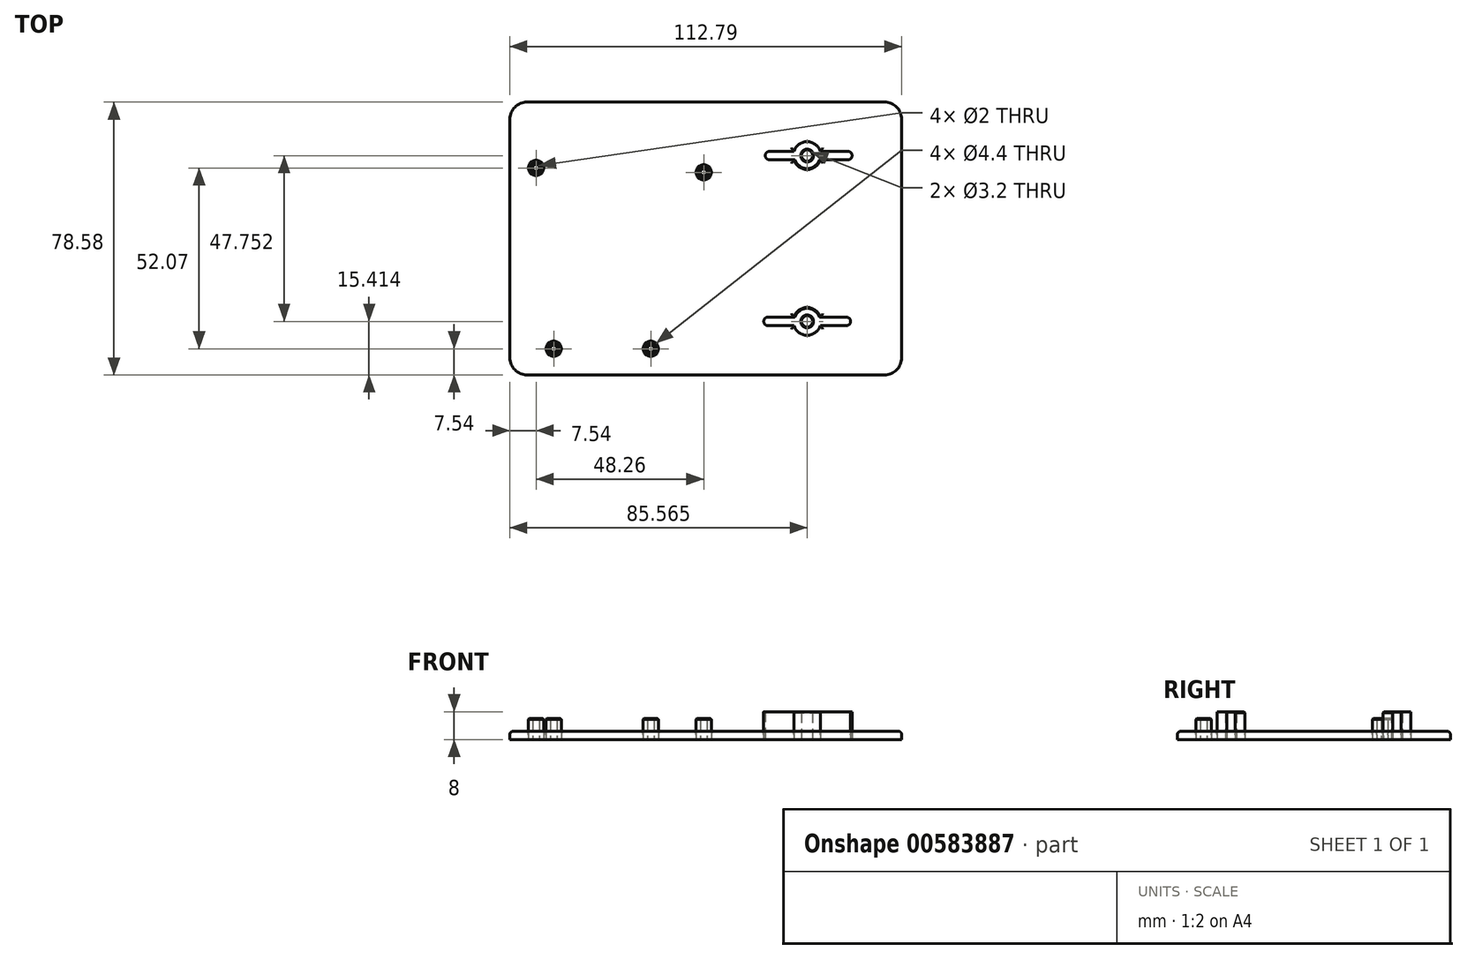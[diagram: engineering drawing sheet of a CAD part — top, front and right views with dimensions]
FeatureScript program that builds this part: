
annotation { "Feature Type Name" : "Feature", "Feature Type Description" : "" }
export const myFeature = defineFeature(function(context is Context, id is Id, definition is map)
    precondition{}
    {
        {
            var Q0;
            Q0=qCreatedBy(makeId("Top.planeOp"),FACE);
            var sketch = newSketch(context, id + "F0", { "sketchPlane" : qUnion([Q0])});
            skLineSegment(sketch, "E0.bottom", {"start": v(0, 0) * mm, "end": v(102.79, 0) * mm});
            skLineSegment(sketch, "E0.top", {"start": v(0, 68.58) * mm, "end": v(102.79, 68.58) * mm});
            skLineSegment(sketch, "E0.left", {"start": v(0, 0) * mm, "end": v(0, 68.58) * mm});
            skLineSegment(sketch, "E0.right", {"start": v(102.79, 0) * mm, "end": v(102.79, 68.58) * mm});
            skLineSegment(sketch, "E1.0", {"start": v(-5, 0) * mm, "end": v(-5, 68.58) * mm});
            skLineSegment(sketch, "E1.1", {"start": v(0, -5) * mm, "end": v(102.79, -5) * mm});
            skLineSegment(sketch, "E1.2", {"start": v(107.79, 0) * mm, "end": v(107.79, 68.58) * mm});
            skLineSegment(sketch, "E1.3", {"start": v(0, 73.58) * mm, "end": v(102.79, 73.58) * mm});
            skCircle(sketch, "E2", {"center": v(2.54, 54.6) * mm, "radius": 1 * mm});
            skCircle(sketch, "E3", {"center": v(50.8, 53.34) * mm, "radius": 1 * mm});
            skCircle(sketch, "E4", {"center": v(35.56, 2.54) * mm, "radius": 1 * mm});
            skCircle(sketch, "E5", {"center": v(7.62, 2.54) * mm, "radius": 1 * mm});
            skLineSegment(sketch, "E6", {"start": v(0, 34.29) * mm, "end": v(102.79, 34.29) * mm, "construction": true});
            skLineSegment(sketch, "E7", {"start": v(58.34, 68.58) * mm, "end": v(58.34, 0) * mm, "construction": true});
            skLineSegment(sketch, "E8", {"start": v(53.34, 68.58) * mm, "end": v(53.34, 0) * mm, "construction": true});
            skLineSegment(sketch, "E9", {"start": v(80.56, 68.58) * mm, "end": v(80.56, 0) * mm, "construction": true});
            skLineSegment(sketch, "E10", {"start": v(26.67, 68.58) * mm, "end": v(26.67, 0) * mm, "construction": true});
            skCircle(sketch, "E11", {"center": v(80.56, 58.17) * mm, "radius": 1.6 * mm});
            skCircle(sketch, "E12", {"center": v(80.56, 10.41) * mm, "radius": 1.6 * mm});
            skLineSegment(sketch, "E13", {"start": v(58.34, 62.87) * mm, "end": v(102.79, 62.87) * mm, "construction": true});
            skLineSegment(sketch, "E14", {"start": v(58.34, 5.72) * mm, "end": v(102.79, 5.72) * mm, "construction": true});
            skPoint(sketch, "E15.visualSharp", {"position": v(-5, 73.58) * mm});
            skArc(sketch, "E15.filletArc", {"start": v(0, 73.58) * mm, "mid": v(-3.54, 72.12) * mm, "end": v(-5, 68.58) * mm});
            skPoint(sketch, "E16.visualSharp", {"position": v(107.79, 73.58) * mm});
            skArc(sketch, "E16.filletArc", {"start": v(107.79, 68.58) * mm, "mid": v(106.33, 72.12) * mm, "end": v(102.79, 73.58) * mm});
            skPoint(sketch, "E17.visualSharp", {"position": v(107.79, -5) * mm});
            skArc(sketch, "E17.filletArc", {"start": v(102.79, -5) * mm, "mid": v(106.33, -3.54) * mm, "end": v(107.79, 0) * mm});
            skPoint(sketch, "E18.visualSharp", {"position": v(-5, -5) * mm});
            skArc(sketch, "E18.filletArc", {"start": v(-5, 0) * mm, "mid": v(-3.54, -3.54) * mm, "end": v(0, -5) * mm});
            skCircle(sketch, "E19.0", {"center": v(2.54, 54.6) * mm, "radius": 2.2 * mm});
            skCircle(sketch, "E20.0", {"center": v(7.62, 2.54) * mm, "radius": 2.2 * mm});
            skCircle(sketch, "E21.0", {"center": v(35.56, 2.54) * mm, "radius": 2.2 * mm});
            skCircle(sketch, "E22.0", {"center": v(50.8, 53.34) * mm, "radius": 2.2 * mm});
            skArc(sketch, "E23.0", {"start": v(84.38, 11.61) * mm, "mid": v(80.56, 14.41) * mm, "end": v(76.75, 11.61) * mm});
            skArc(sketch, "E24.0", {"start": v(76.75, 56.97) * mm, "mid": v(80.56, 54.17) * mm, "end": v(84.38, 56.97) * mm});
            skLineSegment(sketch, "E25.bottom", {"start": v(91.86, 9.21) * mm, "end": v(84.38, 9.21) * mm});
            skLineSegment(sketch, "E25.top", {"start": v(91.86, 11.61) * mm, "end": v(84.38, 11.61) * mm});
            skLineSegment(sketch, "E25.left", {"start": v(93.06, 10.41) * mm, "end": v(93.06, 10.41) * mm});
            skLineSegment(sketch, "E25.right", {"start": v(68.06, 10.41) * mm, "end": v(68.06, 10.41) * mm});
            skArc(sketch, "E26.trimOffspring", {"start": v(76.75, 9.21) * mm, "mid": v(80.56, 6.41) * mm, "end": v(84.38, 9.21) * mm});
            skLineSegment(sketch, "E27.trimOffspring", {"start": v(76.75, 11.61) * mm, "end": v(69.27, 11.61) * mm});
            skLineSegment(sketch, "E28.trimOffspring", {"start": v(76.75, 9.21) * mm, "end": v(69.27, 9.21) * mm});
            skPoint(sketch, "E29.visualSharp", {"position": v(68.06, 11.61) * mm});
            skArc(sketch, "E29.filletArc", {"start": v(69.27, 11.61) * mm, "mid": v(68.42, 11.26) * mm, "end": v(68.06, 10.41) * mm});
            skPoint(sketch, "E30.visualSharp", {"position": v(68.06, 9.21) * mm});
            skArc(sketch, "E30.filletArc", {"start": v(68.06, 10.41) * mm, "mid": v(68.42, 9.57) * mm, "end": v(69.27, 9.21) * mm});
            skPoint(sketch, "E31.visualSharp", {"position": v(93.06, 11.61) * mm});
            skArc(sketch, "E31.filletArc", {"start": v(93.06, 10.41) * mm, "mid": v(92.71, 11.26) * mm, "end": v(91.86, 11.61) * mm});
            skPoint(sketch, "E32.visualSharp", {"position": v(93.06, 9.21) * mm});
            skArc(sketch, "E32.filletArc", {"start": v(91.86, 9.21) * mm, "mid": v(92.71, 9.57) * mm, "end": v(93.06, 10.41) * mm});
            skLineSegment(sketch, "E33.bottom", {"start": v(92.32, 56.97) * mm, "end": v(84.38, 56.97) * mm});
            skLineSegment(sketch, "E33.top", {"start": v(92.32, 59.37) * mm, "end": v(84.38, 59.37) * mm});
            skLineSegment(sketch, "E33.left", {"start": v(93.52, 58.17) * mm, "end": v(93.52, 58.17) * mm});
            skLineSegment(sketch, "E33.right", {"start": v(68.52, 58.17) * mm, "end": v(68.52, 58.17) * mm});
            skPoint(sketch, "E33.middle", {"position": v(81.02, 58.17) * mm});
            skPoint(sketch, "E34.visualSharp", {"position": v(68.52, 59.37) * mm});
            skArc(sketch, "E34.filletArc", {"start": v(69.72, 59.37) * mm, "mid": v(68.87, 59.01) * mm, "end": v(68.52, 58.17) * mm});
            skPoint(sketch, "E35.visualSharp", {"position": v(68.52, 56.97) * mm});
            skArc(sketch, "E35.filletArc", {"start": v(68.52, 58.17) * mm, "mid": v(68.87, 57.32) * mm, "end": v(69.72, 56.97) * mm});
            skPoint(sketch, "E36.visualSharp", {"position": v(93.52, 59.37) * mm});
            skArc(sketch, "E36.filletArc", {"start": v(93.52, 58.17) * mm, "mid": v(93.17, 59.01) * mm, "end": v(92.32, 59.37) * mm});
            skPoint(sketch, "E37.visualSharp", {"position": v(93.52, 56.97) * mm});
            skArc(sketch, "E37.filletArc", {"start": v(92.32, 56.97) * mm, "mid": v(93.17, 57.32) * mm, "end": v(93.52, 58.17) * mm});
            skArc(sketch, "E38.trimOffspring", {"start": v(84.38, 59.37) * mm, "mid": v(80.56, 62.17) * mm, "end": v(76.75, 59.37) * mm});
            skLineSegment(sketch, "E39.trimOffspring", {"start": v(76.75, 56.97) * mm, "end": v(69.72, 56.97) * mm});
            skLineSegment(sketch, "E40.trimOffspring", {"start": v(76.75, 59.37) * mm, "end": v(69.72, 59.37) * mm});
            skSolve(sketch);
        }
        {
            var Q0;
            Q0=makeQuery(id+"F0.imprint","IMPRINT",FACE,{"disambiguationData":[TD([[makeQuery(id+"F0.imprint","IMPRINT",EDGE,{"derivedFrom":sQuery(id+"F0.wireOp",EDGE,"E2")}),-1.0]])]});
            var Q1;
            Q1=makeQuery(id+"F0.imprint","IMPRINT",FACE,{"disambiguationData":[TD([[makeQuery(id+"F0.imprint","IMPRINT",EDGE,{"derivedFrom":sQuery(id+"F0.wireOp",EDGE,"E5")}),-1.0]])]});
            var Q2;
            Q2=makeQuery(id+"F0.imprint","IMPRINT",FACE,{"disambiguationData":[TD([[makeQuery(id+"F0.imprint","IMPRINT",EDGE,{"derivedFrom":sQuery(id+"F0.wireOp",EDGE,"E4")}),-1.0]])]});
            var Q3;
            Q3=makeQuery(id+"F0.imprint","IMPRINT",FACE,{"disambiguationData":[TD([[makeQuery(id+"F0.imprint","IMPRINT",EDGE,{"derivedFrom":sQuery(id+"F0.wireOp",EDGE,"E3")}),-1.0]])]});
            extrude(context, id + "F1", {"entities" : qUnion([Q0, Q1, Q2, Q3]), "flatOperationType" : FlatOperationType.REMOVE, "depth" : 6 * mm, "offsetDistance" : 25 * mm, "domain" : OperationDomain.MODEL});
        }
        {
            var Q0;
            Q0=makeQuery(id+"F0.imprint","IMPRINT",FACE,{"disambiguationData":[TD([[makeQuery(id+"F0.imprint","IMPRINT",EDGE,{"derivedFrom":sQuery(id+"F0.wireOp",EDGE,"E11")}),-1.0]])]});
            var Q1;
            Q1=makeQuery(id+"F0.imprint","IMPRINT",FACE,{"disambiguationData":[TD([[makeQuery(id+"F0.imprint","IMPRINT",EDGE,{"derivedFrom":sQuery(id+"F0.wireOp",EDGE,"E12")}),-1.0]])]});
            extrude(context, id + "F2", {"entities" : qUnion([Q0, Q1]), "flatOperationType" : FlatOperationType.REMOVE, "depth" : 8 * mm, "offsetDistance" : 25 * mm, "domain" : OperationDomain.MODEL});
        }
        {
            var Q0;
            Q0=makeQuery(id+"F0.imprint","IMPRINT",FACE,{"disambiguationData":[TD([[makeQuery(id+"F0.imprint","IMPRINT",EDGE,{"derivedFrom":sQuery(id+"F0.wireOp",EDGE,"E0.bottom")}),-1.0]])]});
            var Q1;
            Q1=makeQuery(id+"F0.imprint","IMPRINT",FACE,{"disambiguationData":[TD([[makeQuery(id+"F0.imprint","IMPRINT",EDGE,{"derivedFrom":sQuery(id+"F0.wireOp",EDGE,"E0.bottom")}),1.0]])]});
            extrude(context, id + "F3", {"entities" : qUnion([Q0, Q1]), "flatOperationType" : FlatOperationType.REMOVE, "depth" : 2.4 * mm, "offsetDistance" : 25 * mm, "domain" : OperationDomain.MODEL});
        }
        {
            var Q0;
            Q0=makeQuery(id+"F1.opExtrude","CAP_EDGE",EDGE,{"disambiguationData":[OSD([sQuery(id+"F0.wireOp",EDGE,"E19.0")])],"isStart":false});
            var Q1;
            Q1=makeQuery(id+"F1.opExtrude","CAP_EDGE",EDGE,{"disambiguationData":[OSD([sQuery(id+"F0.wireOp",EDGE,"E2")])],"isStart":false});
            var Q2;
            Q2=makeQuery(id+"F1.opExtrude","CAP_EDGE",EDGE,{"disambiguationData":[OSD([sQuery(id+"F0.wireOp",EDGE,"E5")])],"isStart":false});
            var Q3;
            Q3=makeQuery(id+"F1.opExtrude","CAP_EDGE",EDGE,{"disambiguationData":[OSD([sQuery(id+"F0.wireOp",EDGE,"E20.0")])],"isStart":false});
            var Q4;
            Q4=makeQuery(id+"F1.opExtrude","CAP_EDGE",EDGE,{"disambiguationData":[OSD([sQuery(id+"F0.wireOp",EDGE,"E4")])],"isStart":false});
            var Q5;
            Q5=makeQuery(id+"F1.opExtrude","CAP_EDGE",EDGE,{"disambiguationData":[OSD([sQuery(id+"F0.wireOp",EDGE,"E21.0")])],"isStart":false});
            var Q6;
            Q6=makeQuery(id+"F1.opExtrude","CAP_EDGE",EDGE,{"disambiguationData":[OSD([sQuery(id+"F0.wireOp",EDGE,"E3")])],"isStart":false});
            var Q7;
            Q7=makeQuery(id+"F1.opExtrude","CAP_EDGE",EDGE,{"disambiguationData":[OSD([sQuery(id+"F0.wireOp",EDGE,"E22.0")])],"isStart":false});
            var Q8;
            Q8=makeQuery(id+"F2.opExtrude","CAP_EDGE",EDGE,{"disambiguationData":[OSD([sQuery(id+"F0.wireOp",EDGE,"E11")])],"isStart":false});
            var Q9;
            Q9=makeQuery(id+"F2.opExtrude","CAP_EDGE",EDGE,{"disambiguationData":[OSD([sQuery(id+"F0.wireOp",EDGE,"E24.0")])],"isStart":false});
            var Q10;
            Q10=makeQuery(id+"F2.opExtrude","CAP_EDGE",EDGE,{"disambiguationData":[OSD([sQuery(id+"F0.wireOp",EDGE,"E23.0")])],"isStart":false});
            var Q11;
            Q11=makeQuery(id+"F2.opExtrude","CAP_EDGE",EDGE,{"disambiguationData":[OSD([sQuery(id+"F0.wireOp",EDGE,"E12")])],"isStart":false});
            chamfer(context, id + "F4", {"entities" : qUnion([Q0, Q1, Q2, Q3, Q4, Q5, Q6, Q7, Q8, Q9, Q10, Q11]), "width" : 0.25 * mm, "tangentPropagation" : true});
        }
        {
            var Q0;
            Q0=makeQuery(id+"F3.opExtrude","CAP_EDGE",EDGE,{"disambiguationData":[OSD([sQuery(id+"F0.wireOp",EDGE,"E19.0")])],"isStart":false});
            fillet(context, id + "F5", {"entities" : qUnion([Q0]), "radius" : 1 * mm, "tangentPropagation" : true, "defaultsChanged" : false, "vertexSettings" : [], "allowEdgeOverflow" : false});
        }
        {
            var Q0;
            Q0=makeQuery(id+"F3.opExtrude","CAP_EDGE",EDGE,{"disambiguationData":[OSD([sQuery(id+"F0.wireOp",EDGE,"E20.0")])],"isStart":false});
            var Q1;
            Q1=makeQuery(id+"F3.opExtrude","CAP_EDGE",EDGE,{"disambiguationData":[OSD([sQuery(id+"F0.wireOp",EDGE,"E21.0")])],"isStart":false});
            var Q2;
            Q2=makeQuery(id+"F3.opExtrude","CAP_EDGE",EDGE,{"disambiguationData":[OSD([sQuery(id+"F0.wireOp",EDGE,"E22.0")])],"isStart":false});
            fillet(context, id + "F6", {"entities" : qUnion([Q0, Q1, Q2]), "radius" : 1 * mm, "tangentPropagation" : true, "defaultsChanged" : false, "vertexSettings" : [], "allowEdgeOverflow" : false});
        }
        {
            var Q0;
            Q0=makeQuery(id+"F3.opExtrude","CAP_FACE",FACE,{"disambiguationData":[OSD([sQuery(id+"F0.wireOp",EDGE,"E1.0"),sQuery(id+"F0.wireOp",EDGE,"E1.1"),sQuery(id+"F0.wireOp",EDGE,"E1.2"),sQuery(id+"F0.wireOp",EDGE,"E1.3"),sQuery(id+"F0.wireOp",EDGE,"E15.filletArc"),sQuery(id+"F0.wireOp",EDGE,"E16.filletArc"),sQuery(id+"F0.wireOp",EDGE,"E17.filletArc"),sQuery(id+"F0.wireOp",EDGE,"E18.filletArc"),sQuery(id+"F0.wireOp",EDGE,"E19.0"),sQuery(id+"F0.wireOp",EDGE,"E20.0"),sQuery(id+"F0.wireOp",EDGE,"E21.0"),sQuery(id+"F0.wireOp",EDGE,"E22.0"),sQuery(id+"F0.wireOp",EDGE,"E23.0"),sQuery(id+"F0.wireOp",EDGE,"E24.0"),sQuery(id+"F0.wireOp",EDGE,"E25.bottom"),sQuery(id+"F0.wireOp",EDGE,"E25.top"),sQuery(id+"F0.wireOp",EDGE,"E26.trimOffspring"),sQuery(id+"F0.wireOp",EDGE,"E27.trimOffspring"),sQuery(id+"F0.wireOp",EDGE,"E28.trimOffspring"),sQuery(id+"F0.wireOp",EDGE,"E29.filletArc"),sQuery(id+"F0.wireOp",EDGE,"E30.filletArc"),sQuery(id+"F0.wireOp",EDGE,"E31.filletArc"),sQuery(id+"F0.wireOp",EDGE,"E32.filletArc"),sQuery(id+"F0.wireOp",EDGE,"E33.bottom"),sQuery(id+"F0.wireOp",EDGE,"E33.top"),sQuery(id+"F0.wireOp",EDGE,"E34.filletArc"),sQuery(id+"F0.wireOp",EDGE,"E35.filletArc"),sQuery(id+"F0.wireOp",EDGE,"E36.filletArc"),sQuery(id+"F0.wireOp",EDGE,"E37.filletArc"),sQuery(id+"F0.wireOp",EDGE,"E38.trimOffspring"),sQuery(id+"F0.wireOp",EDGE,"E39.trimOffspring"),sQuery(id+"F0.wireOp",EDGE,"E40.trimOffspring")])],"isStart":false});
            fillet(context, id + "F7", {"entities" : qUnion([Q0]), "radius" : 1 * mm, "tangentPropagation" : true, "allowEdgeOverflow" : false});
        }
    });
